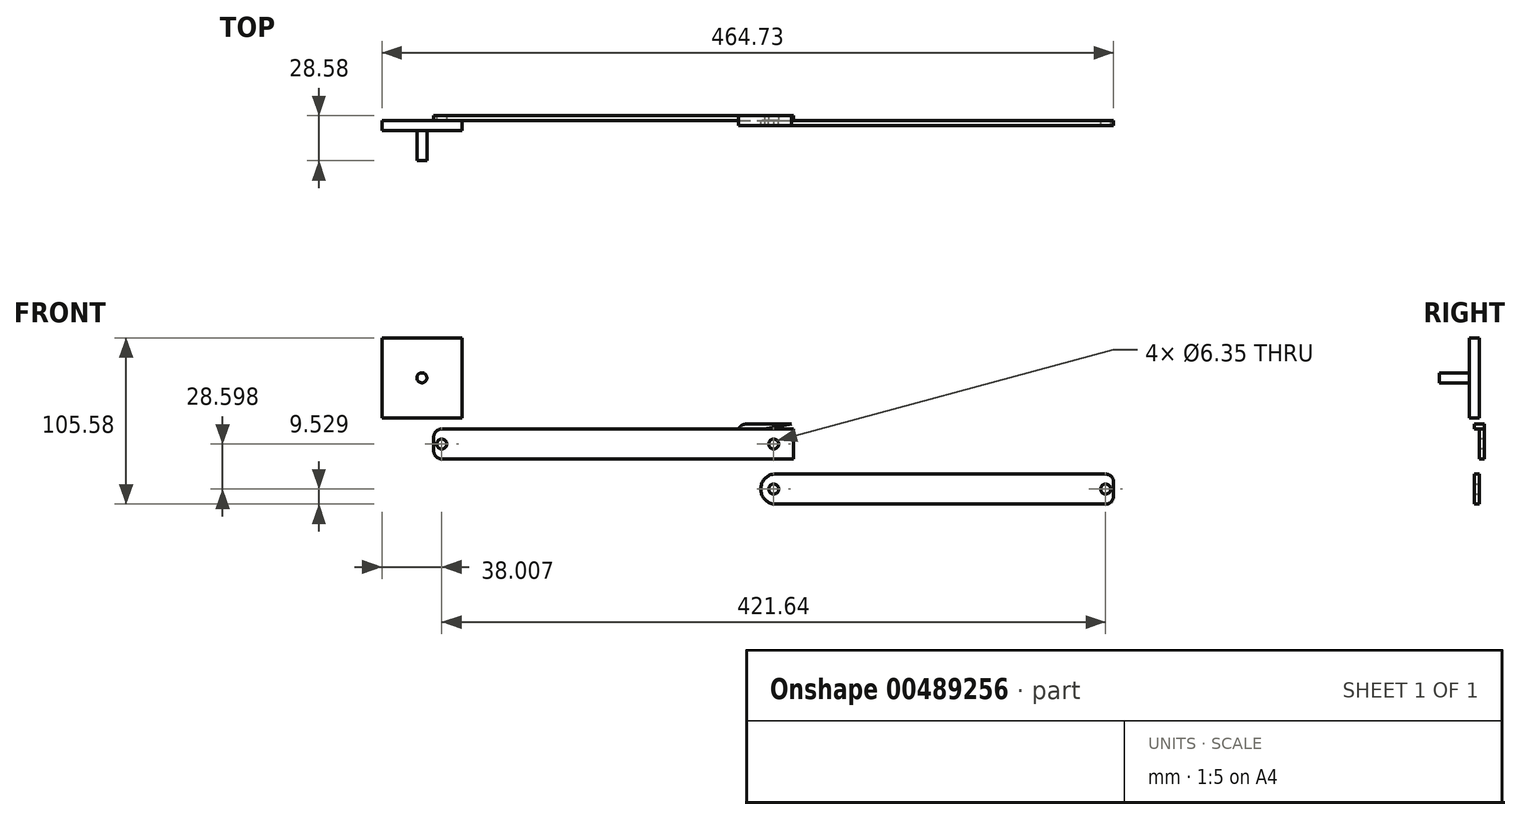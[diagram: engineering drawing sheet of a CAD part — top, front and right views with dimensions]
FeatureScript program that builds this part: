
annotation { "Feature Type Name" : "Feature", "Feature Type Description" : "" }
export const myFeature = defineFeature(function(context is Context, id is Id, definition is map)
    precondition{}
    {
        {
            var Q0;
            Q0=qCreatedBy(makeId("Front.planeOp"),FACE);
            var sketch = newSketch(context, id + "F0", { "sketchPlane" : qUnion([Q0])});
            skLineSegment(sketch, "E0.bottom", {"start": v(-221.25, 12.44) * mm, "end": v(7.35, 12.44) * mm});
            skLineSegment(sketch, "E0.top", {"start": v(-221.25, -6.6) * mm, "end": v(7.35, -6.6) * mm});
            skLineSegment(sketch, "E0.left", {"start": v(-221.25, 12.44) * mm, "end": v(-221.25, -6.6) * mm});
            skLineSegment(sketch, "E0.right", {"start": v(7.35, 12.44) * mm, "end": v(7.35, -6.6) * mm});
            skCircle(sketch, "E1", {"center": v(-5.35, 2.92) * mm, "radius": 3.18 * mm});
            skLineSegment(sketch, "E2.bottom", {"start": v(-18.05, -16.16) * mm, "end": v(210.55, -16.16) * mm});
            skLineSegment(sketch, "E2.top", {"start": v(-18.05, -35.2) * mm, "end": v(210.55, -35.2) * mm});
            skLineSegment(sketch, "E2.left", {"start": v(-18.05, -16.16) * mm, "end": v(-18.05, -35.2) * mm});
            skLineSegment(sketch, "E2.right", {"start": v(210.55, -16.16) * mm, "end": v(210.55, -35.2) * mm});
            skCircle(sketch, "E3", {"center": v(-5.35, -25.68) * mm, "radius": 3.18 * mm});
            skSolve(sketch);
        }
        {
            var Q0;
            Q0=makeQuery(id+"F0.imprint","IMPRINT",FACE,{"disambiguationData":[TD([[makeQuery(id+"F0.imprint","IMPRINT",EDGE,{"derivedFrom":sQuery(id+"F0.wireOp",EDGE,"E0.bottom")}),-1.0]])]});
            extrude(context, id + "F1", {"entities" : qUnion([Q0]), "oppositeDirection" : true, "depth" : 3.17 * mm, "offsetDistance" : 25.4 * mm});
        }
        {
            var Q0;
            Q0=makeQuery(id+"F0.imprint","IMPRINT",FACE,{"disambiguationData":[TD([[makeQuery(id+"F0.imprint","IMPRINT",EDGE,{"derivedFrom":sQuery(id+"F0.wireOp",EDGE,"E2.bottom")}),-1.0]])]});
            extrude(context, id + "F2", {"entities" : qUnion([Q0]), "depth" : 3.17 * mm, "offsetDistance" : 25.4 * mm});
        }
        {
            var Q0;
            Q0=makeQuery(id+"F1.opExtrude","SWEPT_EDGE",EDGE,{"disambiguationData":[OSD([sQuery(id+"F0.wireOp",EDGE,"E0.bottom"),sQuery(id+"F0.wireOp",EDGE,"E0.left")])]});
            var Q1;
            Q1=makeQuery(id+"F1.opExtrude","SWEPT_EDGE",EDGE,{"disambiguationData":[OSD([sQuery(id+"F0.wireOp",EDGE,"E0.top"),sQuery(id+"F0.wireOp",EDGE,"E0.left")])]});
            fillet(context, id + "F3", {"entities" : qUnion([Q0, Q1]), "radius" : 5.08 * mm, "tangentPropagation" : true, "allowEdgeOverflow" : false});
        }
        {
            var Q0;
            Q0=makeQuery(id+"F2.opExtrude","SWEPT_EDGE",EDGE,{"disambiguationData":[OSD([sQuery(id+"F0.wireOp",EDGE,"E2.bottom"),sQuery(id+"F0.wireOp",EDGE,"E2.right")])]});
            var Q1;
            Q1=makeQuery(id+"F2.opExtrude","SWEPT_EDGE",EDGE,{"disambiguationData":[OSD([sQuery(id+"F0.wireOp",EDGE,"E2.top"),sQuery(id+"F0.wireOp",EDGE,"E2.right")])]});
            fillet(context, id + "F4", {"entities" : qUnion([Q0, Q1]), "radius" : 5.08 * mm, "tangentPropagation" : true, "allowEdgeOverflow" : false});
        }
        {
            var Q0;
            Q0=makeQuery(id+"F1.opExtrude","SWEPT_FACE",FACE,{"disambiguationData":[OSD([sQuery(id+"F0.wireOp",EDGE,"E0.bottom")])]});
            var sketch = newSketch(context, id + "F5", { "sketchPlane" : qUnion([Q0])});
            skLineSegment(sketch, "E4.bottom", {"start": v(10.52, 3.17) * mm, "end": v(-27.58, 3.17) * mm});
            skLineSegment(sketch, "E4.top", {"start": v(10.52, -3.17) * mm, "end": v(-27.58, -3.17) * mm});
            skLineSegment(sketch, "E4.left", {"start": v(10.52, 3.17) * mm, "end": v(10.52, -3.17) * mm});
            skLineSegment(sketch, "E4.right", {"start": v(-27.58, 3.17) * mm, "end": v(-27.58, -3.17) * mm});
            skSolve(sketch);
        }
        {
            var Q0;
            {var subQ0=sQuery(id+"F5.wireOp",EDGE,"E4.bottom");Q0=makeQuery(id+"F5.imprint","IMPRINT",FACE,{"disambiguationData":[TD([[makeQuery(id+"F5.imprint","IMPRINT",EDGE,{"derivedFrom":subQ0}),-1.0]])]});}
            var Q1;
            {var subQ0=sQuery(id+"F5.wireOp",EDGE,"E4.top");Q1=makeQuery(id+"F5.imprint","IMPRINT",FACE,{"disambiguationData":[TD([[makeQuery(id+"F5.imprint","IMPRINT",EDGE,{"derivedFrom":subQ0}),-1.0]])]});}
            extrude(context, id + "F6", {"entities" : qUnion([Q0, Q1]), "operationType" : NewBodyOperationType.ADD, "depth" : 3.17 * mm, "offsetDistance" : 25.4 * mm});
        }
        {
            var Q0;
            Q0=makeQuery(id+"F6.opExtrude","CAP_EDGE",EDGE,{"disambiguationData":[OSD([sQuery(id+"F5.wireOp",EDGE,"E4.right")])],"isStart":false});
            var Q1;
            Q1=makeQuery(id+"F6.opExtrude","CAP_EDGE",EDGE,{"disambiguationData":[OSD([sQuery(id+"F5.wireOp",EDGE,"E4.left")])],"isStart":false});
            fillet(context, id + "F7", {"entities" : qUnion([Q0, Q1]), "radius" : 5.08 * mm, "tangentPropagation" : true, "allowEdgeOverflow" : false});
        }
        {
            var Q0;
            Q0=makeQuery(id+"F6.opExtrude","SWEPT_FACE",FACE,{"disambiguationData":[OSD([sQuery(id+"F5.wireOp",EDGE,"E4.top")])]});
            var sketch = newSketch(context, id + "F8", { "sketchPlane" : qUnion([Q0])});
            skLineSegment(sketch, "E5", {"start": v(-11.16, 12.44) * mm, "end": v(5.81, 15.62) * mm});
            skLineSegment(sketch, "E6", {"start": v(-11.16, 12.44) * mm, "end": v(-11.16, 15.62) * mm, "construction": true});
            skSolve(sketch);
        }
        {
            var Q0;
            {var subQ0=sQuery(id+"F8.wireOp",EDGE,"E5");Q0=makeQuery(id+"F8.imprint","IMPRINT",FACE,{"disambiguationData":[TD([[makeQuery(id+"F8.imprint","IMPRINT",EDGE,{"derivedFrom":subQ0}),-1.0]])]});}
            extrude(context, id + "F9", {"entities" : qUnion([Q0]), "operationType" : NewBodyOperationType.REMOVE, "oppositeDirection" : true, "depth" : 25.4 * mm, "offsetDistance" : 25.4 * mm});
        }
        {
            var Q0;
            Q0=makeQuery(id+"F2.opExtrude","CAP_FACE",FACE,{"disambiguationData":[OSD([sQuery(id+"F0.wireOp",EDGE,"E2.bottom"),sQuery(id+"F0.wireOp",EDGE,"E2.top"),sQuery(id+"F0.wireOp",EDGE,"E2.left"),sQuery(id+"F0.wireOp",EDGE,"E2.right"),sQuery(id+"F0.wireOp",EDGE,"E3")])],"isStart":false});
            var sketch = newSketch(context, id + "F10", { "sketchPlane" : qUnion([Q0])});
            skArc(sketch, "E7", {"start": v(-5.35, -16.16) * mm, "mid": v(-13.6, -25.68) * mm, "end": v(-5.35, -35.2) * mm});
            skSolve(sketch);
        }
        {
            var Q0;
            {var subQ0=sQuery(id+"F10.wireOp",EDGE,"E7");Q0=makeQuery(id+"F10.imprint","IMPRINT",FACE,{"disambiguationData":[TD([[makeQuery(id+"F10.imprint","IMPRINT",EDGE,{"derivedFrom":subQ0}),-1.0]])]});}
            extrude(context, id + "F11", {"entities" : qUnion([Q0]), "operationType" : NewBodyOperationType.REMOVE, "oppositeDirection" : true, "depth" : 25.4 * mm, "offsetDistance" : 25.4 * mm});
        }
        {
            var Q0;
            Q0=makeQuery(id+"F1.opExtrude","CAP_FACE",FACE,{"disambiguationData":[OSD([sQuery(id+"F0.wireOp",EDGE,"E0.bottom"),sQuery(id+"F0.wireOp",EDGE,"E0.top"),sQuery(id+"F0.wireOp",EDGE,"E0.left"),sQuery(id+"F0.wireOp",EDGE,"E0.right"),sQuery(id+"F0.wireOp",EDGE,"E1")])],"isStart":true});
            var sketch = newSketch(context, id + "F12", { "sketchPlane" : qUnion([Q0])});
            skCircle(sketch, "E8", {"center": v(-216.17, 2.92) * mm, "radius": 3.18 * mm});
            skPoint(sketch, "E8.centerSnap0", {"position": v(-221.25, 2.92) * mm});
            skSolve(sketch);
        }
        {
            var Q0;
            Q0=makeQuery(id+"F12.imprint","IMPRINT",FACE,{"disambiguationData":[TD([[makeQuery(id+"F12.imprint","IMPRINT",EDGE,{"derivedFrom":sQuery(id+"F12.wireOp",EDGE,"E8")}),1.0]])]});
            extrude(context, id + "F13", {"entities" : qUnion([Q0]), "operationType" : NewBodyOperationType.REMOVE, "endBound" : BoundingType.THROUGH_ALL, "oppositeDirection" : true, "depth" : 25.4 * mm, "offsetDistance" : 25.4 * mm});
        }
        {
            var Q0;
            Q0=makeQuery(id+"F2.opExtrude","CAP_FACE",FACE,{"disambiguationData":[OSD([sQuery(id+"F0.wireOp",EDGE,"E2.bottom"),sQuery(id+"F0.wireOp",EDGE,"E2.top"),sQuery(id+"F0.wireOp",EDGE,"E2.left"),sQuery(id+"F0.wireOp",EDGE,"E2.right"),sQuery(id+"F0.wireOp",EDGE,"E3")])],"isStart":false});
            var sketch = newSketch(context, id + "F14", { "sketchPlane" : qUnion([Q0])});
            skCircle(sketch, "E9", {"center": v(205.47, -25.68) * mm, "radius": 3.18 * mm});
            skPoint(sketch, "E9.centerSnap0", {"position": v(210.55, -25.68) * mm});
            skSolve(sketch);
        }
        {
            var Q0;
            Q0=makeQuery(id+"F14.imprint","IMPRINT",FACE,{"disambiguationData":[TD([[makeQuery(id+"F14.imprint","IMPRINT",EDGE,{"derivedFrom":sQuery(id+"F14.wireOp",EDGE,"E9")}),1.0]])]});
            extrude(context, id + "F15", {"entities" : qUnion([Q0]), "operationType" : NewBodyOperationType.REMOVE, "endBound" : BoundingType.THROUGH_ALL, "oppositeDirection" : true, "depth" : 25.4 * mm, "offsetDistance" : 25.4 * mm});
        }
        {
            var Q0;
            Q0=qCreatedBy(makeId("Front.planeOp"),FACE);
            var sketch = newSketch(context, id + "F16", { "sketchPlane" : qUnion([Q0])});
            skLineSegment(sketch, "E10.bottom", {"start": v(-254.18, 70.37) * mm, "end": v(-203.38, 70.37) * mm});
            skLineSegment(sketch, "E10.top", {"start": v(-254.18, 19.57) * mm, "end": v(-203.38, 19.57) * mm});
            skLineSegment(sketch, "E10.left", {"start": v(-254.18, 70.37) * mm, "end": v(-254.18, 19.57) * mm});
            skLineSegment(sketch, "E10.right", {"start": v(-203.38, 70.37) * mm, "end": v(-203.38, 19.57) * mm});
            skCircle(sketch, "E11", {"center": v(-228.78, 44.97) * mm, "radius": 3.18 * mm});
            skPoint(sketch, "E11.centerSnap0", {"position": v(-203.38, 44.97) * mm});
            skPoint(sketch, "E11.centerSnap1", {"position": v(-228.78, 70.37) * mm});
            skSolve(sketch);
        }
        {
            var Q0;
            Q0=makeQuery(id+"F16.imprint","IMPRINT",FACE,{"disambiguationData":[TD([[makeQuery(id+"F16.imprint","IMPRINT",EDGE,{"derivedFrom":sQuery(id+"F16.wireOp",EDGE,"E10.bottom")}),-1.0]])]});
            extrude(context, id + "F17", {"entities" : qUnion([Q0]), "depth" : 6.35 * mm, "offsetDistance" : 25.4 * mm});
        }
        {
            var Q0;
            Q0=makeQuery(id+"F16.imprint","IMPRINT",FACE,{"disambiguationData":[TD([[makeQuery(id+"F16.imprint","IMPRINT",EDGE,{"derivedFrom":sQuery(id+"F16.wireOp",EDGE,"E11")}),1.0]])]});
            extrude(context, id + "F18", {"entities" : qUnion([Q0]), "operationType" : NewBodyOperationType.ADD, "depth" : 25.4 * mm, "offsetDistance" : 25.4 * mm});
        }
    });
